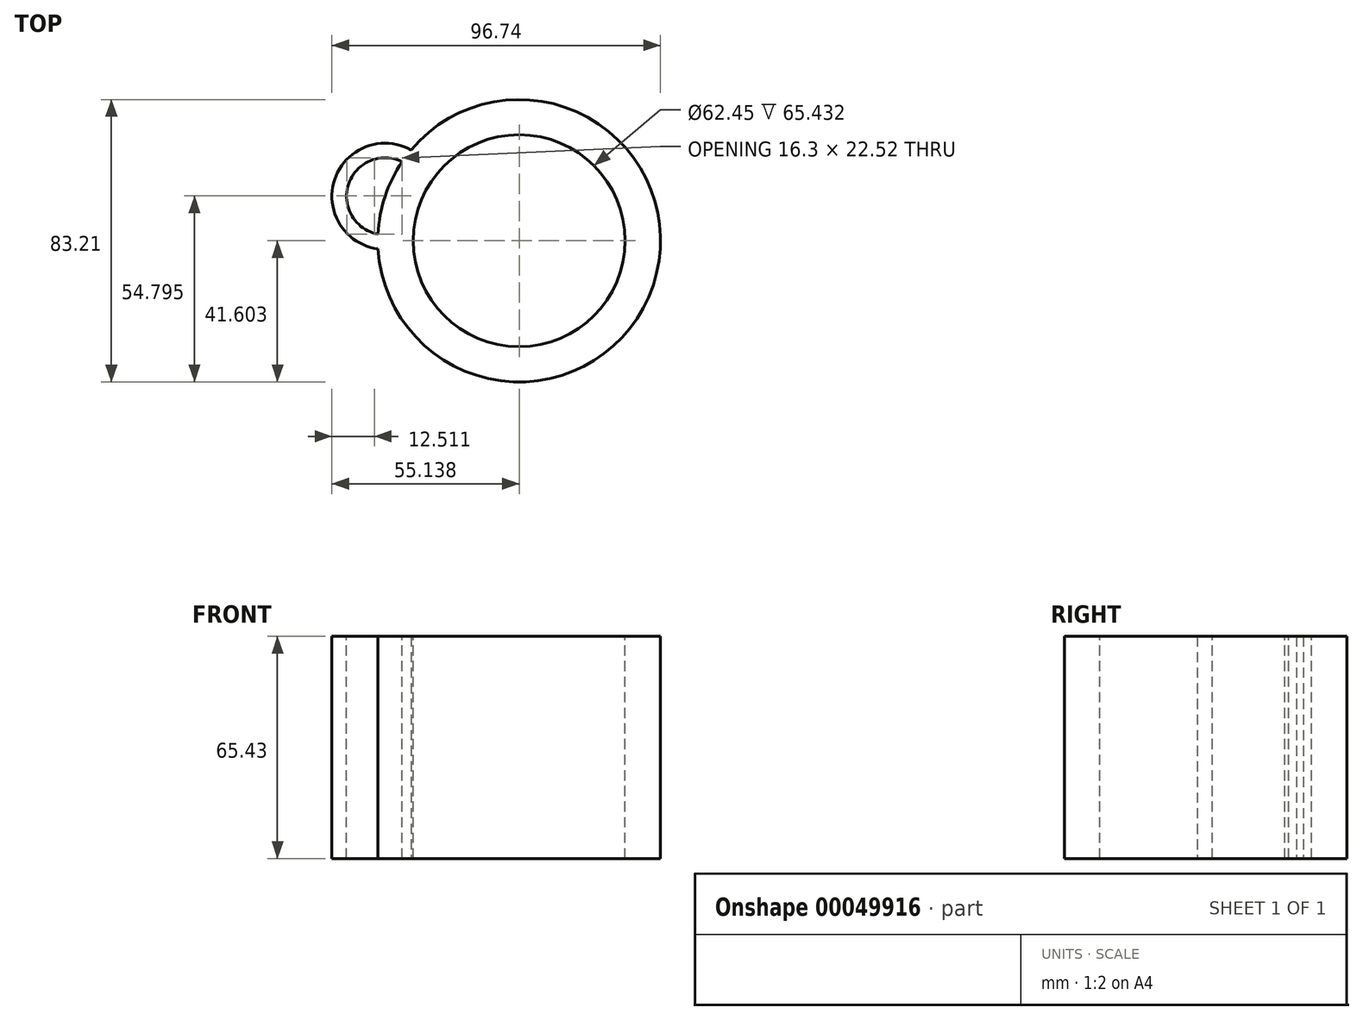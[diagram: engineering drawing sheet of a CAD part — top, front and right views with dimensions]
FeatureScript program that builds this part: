
annotation { "Feature Type Name" : "Feature", "Feature Type Description" : "" }
export const myFeature = defineFeature(function(context is Context, id is Id, definition is map)
    precondition{}
    {
        {
            var Q0;
            Q0=qCreatedBy(makeId("Top.planeOp"),FACE);
            var sketch = newSketch(context, id + "F0", { "sketchPlane" : qUnion([Q0])});
            skArc(sketch, "E0", {"start": v(-83.59, -47.62) * mm, "mid": v(-2.56, -58.3) * mm, "end": v(-73.9, -18.43) * mm});
            skArc(sketch, "E1", {"start": v(-73.9, -18.43) * mm, "mid": v(-96.4, -27.17) * mm, "end": v(-83.59, -47.62) * mm});
            skSolve(sketch);
        }
        {
            var Q0;
            Q0=makeQuery(id+"F0.imprint","IMPRINT",FACE,{"disambiguationData":[TD([[makeQuery(id+"F0.imprint","IMPRINT",EDGE,{"derivedFrom":sQuery(id+"F0.wireOp",EDGE,"E0")}),1.0]])]});
            extrude(context, id + "F1", {"entities" : qUnion([Q0]), "depth" : 65.43 * mm});
        }
        {
            var Q0;
            Q0=makeQuery(id+"F1.opExtrude","CAP_FACE",FACE,{"disambiguationData":[OSD([sQuery(id+"F0.wireOp",EDGE,"E0"),sQuery(id+"F0.wireOp",EDGE,"E1")])],"isStart":false});
            var sketch = newSketch(context, id + "F2", { "sketchPlane" : qUnion([Q0])});
            skCircle(sketch, "E2", {"center": v(-42.05, -45.2) * mm, "radius": 31.22 * mm});
            skSolve(sketch);
        }
        {
            var Q0;
            Q0 = qSketchRegion(id + "F2", true);
            extrude(context, id + "F3", {"entities" : qUnion([Q0]), "operationType" : NewBodyOperationType.REMOVE, "oppositeDirection" : true, "depth" : 109.99 * mm});
        }
        {
            var Q0;
            Q0=makeQuery(id+"F1.opExtrude","CAP_FACE",FACE,{"disambiguationData":[OSD([sQuery(id+"F0.wireOp",EDGE,"E0"),sQuery(id+"F0.wireOp",EDGE,"E1")])],"isStart":false});
            var sketch = newSketch(context, id + "F4", { "sketchPlane" : qUnion([Q0])});
            skArc(sketch, "E3", {"start": v(-76.53, -21.9) * mm, "mid": v(-92.32, -28.52) * mm, "end": v(-83.61, -43.26) * mm});
            skArc(sketch, "E4", {"start": v(-76.53, -21.9) * mm, "mid": v(-81.54, -32.1) * mm, "end": v(-83.61, -43.26) * mm});
            skSolve(sketch);
        }
        {
            var Q0;
            Q0=makeQuery(id+"F4.imprint","IMPRINT",FACE,{"disambiguationData":[TD([[makeQuery(id+"F4.imprint","IMPRINT",EDGE,{"derivedFrom":sQuery(id+"F4.wireOp",EDGE,"E3")}),1.0]])]});
            var Q1;
            Q1=sQuery(id+"F4.wireOp",EDGE,"E3");
            var Q2;
            Q2=sQuery(id+"F4.wireOp",EDGE,"E4");
            extrude(context, id + "F5", {"entities" : qUnion([Q0]), "operationType" : NewBodyOperationType.REMOVE, "surfaceEntities" : qUnion([Q1, Q2]), "oppositeDirection" : true, "depth" : 101.7 * mm});
        }
    });
